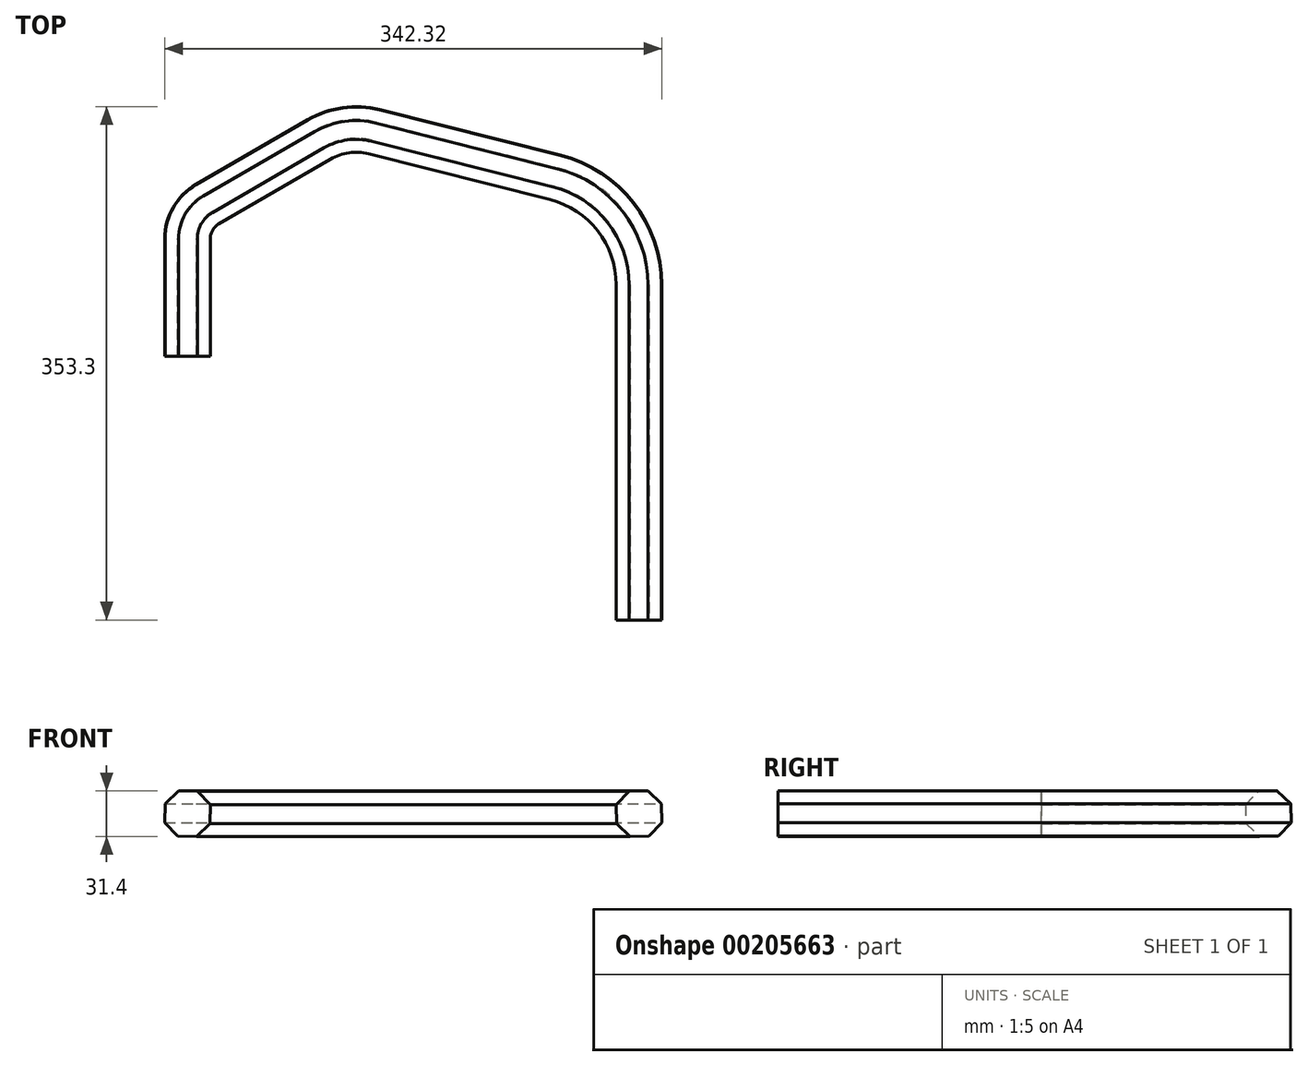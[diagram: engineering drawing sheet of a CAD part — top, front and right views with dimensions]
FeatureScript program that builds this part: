
annotation { "Feature Type Name" : "Feature", "Feature Type Description" : "" }
export const myFeature = defineFeature(function(context is Context, id is Id, definition is map)
    precondition{}
    {
        {
            var Q0;
            Q0=qCreatedBy(makeId("Top.planeOp"),FACE);
            var sketch = newSketch(context, id + "F0", { "sketchPlane" : qUnion([Q0])});
            skLineSegment(sketch, "E0", {"start": v(0, 0) * mm, "end": v(95.6, 0) * mm});
            skCircle(sketch, "E1.cCircle", {"center": v(41, 39.58) * mm, "radius": 20.22 * mm, "construction": true});
            skLineSegment(sketch, "E1.0", {"start": v(16.15, 36.83) * mm, "end": v(30.7, 62.36) * mm});
            skLineSegment(sketch, "E1.1", {"start": v(30.7, 62.36) * mm, "end": v(59.48, 56.41) * mm});
            skLineSegment(sketch, "E1.2", {"start": v(59.48, 56.41) * mm, "end": v(62.71, 27.2) * mm});
            skLineSegment(sketch, "E1.3", {"start": v(62.71, 27.2) * mm, "end": v(35.94, 15.1) * mm});
            skLineSegment(sketch, "E1.4", {"start": v(35.94, 15.1) * mm, "end": v(16.15, 36.83) * mm});
            skPoint(sketch, "E1.0.midPoint", {"position": v(23.43, 49.6) * mm});
            skSolve(sketch);
        }
        {
            var Q0;
            Q0=qCreatedBy(makeId("Top.planeOp"),FACE);
            var sketch = newSketch(context, id + "F1", { "sketchPlane" : qUnion([Q0])});
            skLineSegment(sketch, "E2", {"start": v(0, 0) * mm, "end": v(1232.23, 0) * mm});
            skLineSegment(sketch, "E3", {"start": v(481, 125.2) * mm, "end": v(481, 526.86) * mm});
            skLineSegment(sketch, "E4", {"start": v(481, 526.86) * mm, "end": v(1145.45, 526.86) * mm});
            skLineSegment(sketch, "E5", {"start": v(1145.45, 526.86) * mm, "end": v(1145.45, 417.77) * mm});
            skLineSegment(sketch, "E6", {"start": v(1145.45, 417.77) * mm, "end": v(622.31, 417.77) * mm});
            skLineSegment(sketch, "E7", {"start": v(622.31, 417.77) * mm, "end": v(622.31, 132.64) * mm});
            skLineSegment(sketch, "E8", {"start": v(622.31, 132.64) * mm, "end": v(481, 125.2) * mm});
            skSolve(sketch);
        }
        {
            var Q0;
            Q0=qCreatedBy(makeId("Front.planeOp"),FACE);
            var sketch = newSketch(context, id + "F2", { "sketchPlane" : qUnion([Q0])});
            skCircle(sketch, "E9.cCircle", {"center": v(0, 0) * mm, "radius": 15.57 * mm, "construction": true});
            skLineSegment(sketch, "E9.0", {"start": v(-15.42, 6.78) * mm, "end": v(-6.11, 15.7) * mm});
            skLineSegment(sketch, "E9.1", {"start": v(-6.11, 15.7) * mm, "end": v(6.78, 15.42) * mm});
            skLineSegment(sketch, "E9.2", {"start": v(6.78, 15.42) * mm, "end": v(15.7, 6.11) * mm});
            skLineSegment(sketch, "E9.3", {"start": v(15.7, 6.11) * mm, "end": v(15.42, -6.78) * mm});
            skLineSegment(sketch, "E9.4", {"start": v(15.42, -6.78) * mm, "end": v(6.11, -15.7) * mm});
            skLineSegment(sketch, "E9.5", {"start": v(6.11, -15.7) * mm, "end": v(-6.78, -15.42) * mm});
            skLineSegment(sketch, "E9.6", {"start": v(-6.78, -15.42) * mm, "end": v(-15.7, -6.11) * mm});
            skLineSegment(sketch, "E9.7", {"start": v(-15.7, -6.11) * mm, "end": v(-15.42, 6.78) * mm});
            skPoint(sketch, "E9.0.midPoint", {"position": v(-10.77, 11.24) * mm});
            skSolve(sketch);
        }
        {
            var Q0;
            Q0=qCreatedBy(makeId("Top.planeOp"),FACE);
            var sketch = newSketch(context, id + "F3", { "sketchPlane" : qUnion([Q0])});
            skLineSegment(sketch, "E10", {"start": v(0, 0) * mm, "end": v(0, 80.97) * mm});
            skLineSegment(sketch, "E11", {"start": v(13.8, 104.88) * mm, "end": v(90.64, 149.35) * mm});
            skLineSegment(sketch, "E12", {"start": v(128.5, 154.64) * mm, "end": v(253.32, 123.2) * mm});
            skLineSegment(sketch, "E13", {"start": v(310.92, 49.31) * mm, "end": v(310.92, -181.42) * mm});
            skPoint(sketch, "E14.visualSharp", {"position": v(0, 96.9) * mm});
            skArc(sketch, "E14.filletArc", {"start": v(13.8, 104.88) * mm, "mid": v(3.7, 94.77) * mm, "end": v(0, 80.97) * mm});
            skPoint(sketch, "E15.visualSharp", {"position": v(108.5, 159.68) * mm});
            skArc(sketch, "E15.filletArc", {"start": v(128.5, 154.64) * mm, "mid": v(109.05, 155.7) * mm, "end": v(90.64, 149.35) * mm});
            skPoint(sketch, "E16.visualSharp", {"position": v(310.92, 108.7) * mm});
            skArc(sketch, "E16.filletArc", {"start": v(310.92, 49.31) * mm, "mid": v(294.82, 96.16) * mm, "end": v(253.32, 123.2) * mm});
            skSolve(sketch);
        }
        {
            var Q0;
            Q0=makeQuery(id+"F2.imprint","IMPRINT",FACE,{"disambiguationData":[TD([[makeQuery(id+"F2.imprint","IMPRINT",EDGE,{"derivedFrom":sQuery(id+"F2.wireOp",EDGE,"E9.0")}),-1.0]])]});
            var Q1;
            Q1=sQuery(id+"F3.wireOp",EDGE,"E10");
            var Q2;
            Q2=sQuery(id+"F3.wireOp",EDGE,"E14.filletArc");
            var Q3;
            Q3=sQuery(id+"F3.wireOp",EDGE,"E11");
            var Q4;
            Q4=sQuery(id+"F3.wireOp",EDGE,"E15.filletArc");
            var Q5;
            Q5=sQuery(id+"F3.wireOp",EDGE,"E12");
            var Q6;
            Q6=sQuery(id+"F3.wireOp",EDGE,"E16.filletArc");
            var Q7;
            Q7=sQuery(id+"F3.wireOp",EDGE,"E13");
            sweep(context, id + "F4", {"profiles" : qUnion([Q0]), "path" : qUnion([Q1, Q2, Q3, Q4, Q5, Q6, Q7])});
        }
    });
